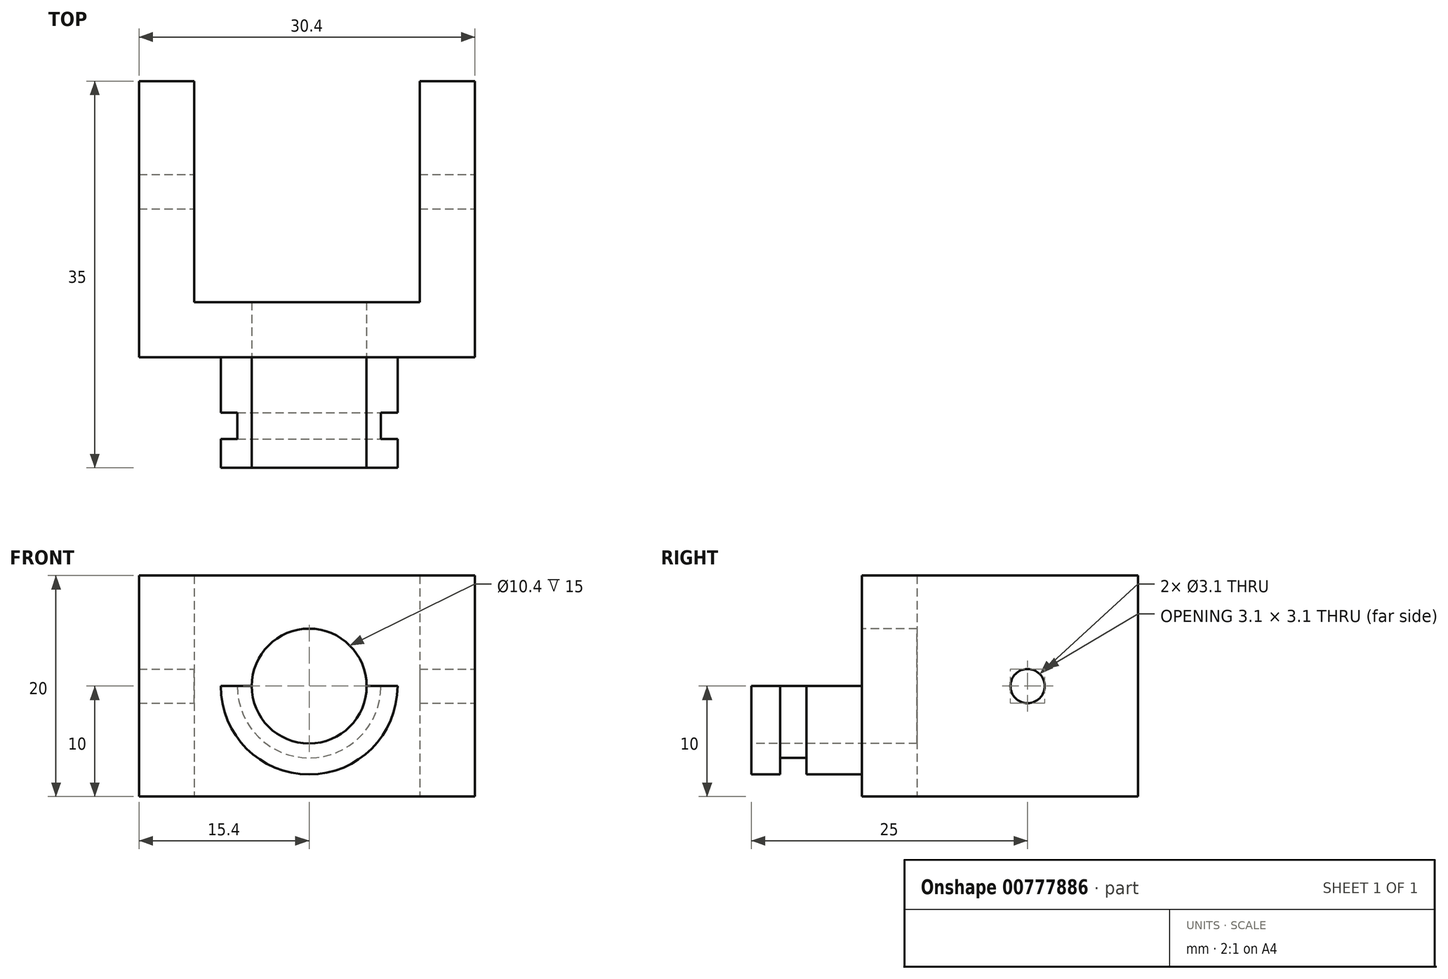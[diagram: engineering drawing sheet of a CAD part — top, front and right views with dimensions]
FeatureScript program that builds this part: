
annotation { "Feature Type Name" : "Feature", "Feature Type Description" : "" }
export const myFeature = defineFeature(function(context is Context, id is Id, definition is map)
    precondition{}
    {
        {
            var Q0;
            Q0=qCreatedBy(makeId("Top.planeOp"),FACE);
            var sketch = newSketch(context, id + "F0", { "sketchPlane" : qUnion([Q0])});
            skLineSegment(sketch, "E0", {"start": v(0, 0) * mm, "end": v(0, 25) * mm});
            skLineSegment(sketch, "E1", {"start": v(0, 25) * mm, "end": v(5, 25) * mm});
            skLineSegment(sketch, "E2", {"start": v(5, 25) * mm, "end": v(5, 5) * mm});
            skLineSegment(sketch, "E3", {"start": v(5, 5) * mm, "end": v(25.4, 5) * mm});
            skLineSegment(sketch, "E4", {"start": v(25.4, 5) * mm, "end": v(25.4, 25) * mm});
            skLineSegment(sketch, "E5", {"start": v(25.4, 25) * mm, "end": v(30.4, 25) * mm});
            skLineSegment(sketch, "E6", {"start": v(30.4, 25) * mm, "end": v(30.4, 0) * mm});
            skLineSegment(sketch, "E7", {"start": v(30.4, 0) * mm, "end": v(0, 0) * mm});
            skSolve(sketch);
        }
        {
            var Q0;
            Q0 = qSketchRegion(id + "F0", true);
            extrude(context, id + "F1", {"entities" : qUnion([Q0]), "depth" : 20 * mm, "offsetDistance" : 25 * mm});
        }
        {
            var Q0;
            Q0=makeQuery(id+"F1.opExtrude","SWEPT_FACE",FACE,{"disambiguationData":[OSD([sQuery(id+"F0.wireOp",EDGE,"E7")])]});
            var sketch = newSketch(context, id + "F2", { "sketchPlane" : qUnion([Q0])});
            skCircle(sketch, "E8", {"center": v(15.4, 10) * mm, "radius": 5.2 * mm});
            skSolve(sketch);
        }
        {
            var Q0;
            Q0 = qSketchRegion(id + "F2", true);
            extrude(context, id + "F3", {"entities" : qUnion([Q0]), "operationType" : NewBodyOperationType.REMOVE, "oppositeDirection" : true, "depth" : 25 * mm, "offsetDistance" : 25 * mm});
        }
        {
            var Q0;
            Q0=makeQuery(id+"F1.opExtrude","SWEPT_FACE",FACE,{"disambiguationData":[OSD([sQuery(id+"F0.wireOp",EDGE,"E7")])]});
            var sketch = newSketch(context, id + "F4", { "sketchPlane" : qUnion([Q0])});
            skArc(sketch, "E9", {"start": v(7.4, 10) * mm, "mid": v(15.4, 2) * mm, "end": v(23.4, 10) * mm});
            skArc(sketch, "E10", {"start": v(10.2, 10) * mm, "mid": v(15.4, 4.8) * mm, "end": v(20.6, 10) * mm});
            skLineSegment(sketch, "E11", {"start": v(20.6, 10) * mm, "end": v(23.4, 10) * mm});
            skLineSegment(sketch, "E12", {"start": v(10.2, 10) * mm, "end": v(7.4, 10) * mm});
            skSolve(sketch);
        }
        {
            var Q0;
            Q0 = qSketchRegion(id + "F4", true);
            extrude(context, id + "F5", {"entities" : qUnion([Q0]), "operationType" : NewBodyOperationType.ADD, "depth" : 10 * mm, "offsetDistance" : 25 * mm});
        }
        {
            var Q0;
            Q0=makeQuery(id+"F1.opExtrude","SWEPT_FACE",FACE,{"disambiguationData":[OSD([sQuery(id+"F0.wireOp",EDGE,"E7")])]});
            cPlane(context, id + "F6", {"entities" : qUnion([Q0]), "cplaneType" : CPlaneType.OFFSET, "offset" : 5 * mm, "width" : 150 * mm, "height" : 150 * mm});
        }
        {
            var Q0;
            Q0=qCreatedBy(id+"F6.planeOp",FACE);
            var sketch = newSketch(context, id + "F7", { "sketchPlane" : qUnion([Q0])});
            skLineSegment(sketch, "E13", {"start": v(21.9, 10) * mm, "end": v(23.4, 10) * mm});
            skArc(sketch, "E14", {"start": v(8.9, 10) * mm, "mid": v(15.4, 3.5) * mm, "end": v(21.9, 10) * mm});
            skArc(sketch, "E15", {"start": v(7.4, 10) * mm, "mid": v(15.4, 2) * mm, "end": v(23.4, 10) * mm});
            skLineSegment(sketch, "E16", {"start": v(8.9, 10) * mm, "end": v(7.4, 10) * mm});
            skSolve(sketch);
        }
        {
            var Q0;
            Q0 = qSketchRegion(id + "F7", true);
            extrude(context, id + "F8", {"entities" : qUnion([Q0]), "operationType" : NewBodyOperationType.REMOVE, "depth" : 2.4 * mm, "offsetDistance" : 25 * mm});
        }
        {
            var Q0;
            Q0=makeQuery(id+"F1.opExtrude","SWEPT_FACE",FACE,{"disambiguationData":[OSD([sQuery(id+"F0.wireOp",EDGE,"E6")])]});
            var sketch = newSketch(context, id + "F9", { "sketchPlane" : qUnion([Q0])});
            skCircle(sketch, "E17", {"center": v(15, 10) * mm, "radius": 1.55 * mm});
            skSolve(sketch);
        }
        {
            var Q0;
            Q0 = qSketchRegion(id + "F9", true);
            extrude(context, id + "F10", {"entities" : qUnion([Q0]), "operationType" : NewBodyOperationType.REMOVE, "oppositeDirection" : true, "depth" : 40 * mm, "offsetDistance" : 25 * mm});
        }
    });
